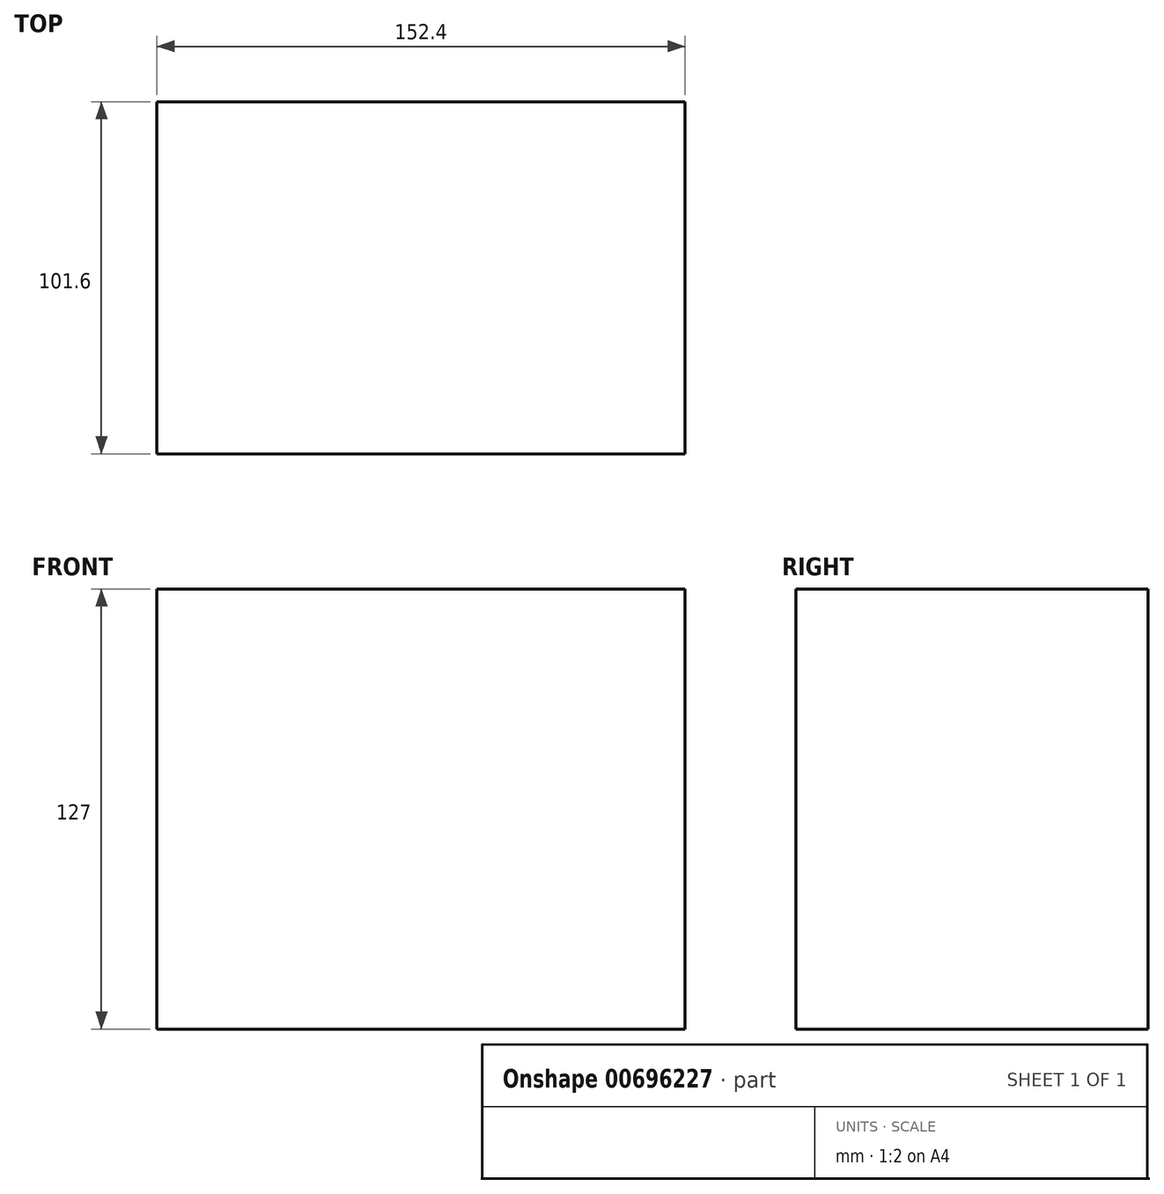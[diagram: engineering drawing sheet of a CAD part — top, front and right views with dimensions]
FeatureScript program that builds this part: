
annotation { "Feature Type Name" : "Feature", "Feature Type Description" : "" }
export const myFeature = defineFeature(function(context is Context, id is Id, definition is map)
    precondition{}
    {
        {
            var Q0;
            Q0=qCreatedBy(makeId("Front.planeOp"),FACE);
            var sketch = newSketch(context, id + "F0", { "sketchPlane" : qUnion([Q0])});
            skLineSegment(sketch, "E0", {"start": v(-76.03, 0) * mm, "end": v(76.37, 0) * mm});
            skLineSegment(sketch, "E1", {"start": v(-76.03, 0) * mm, "end": v(-76.03, 127) * mm});
            skLineSegment(sketch, "E2", {"start": v(-76.03, 127) * mm, "end": v(76.37, 127) * mm});
            skLineSegment(sketch, "E3", {"start": v(76.37, 127) * mm, "end": v(76.37, 0) * mm});
            skSolve(sketch);
        }
        {
            var Q0;
            Q0=makeQuery(id+"F0.imprint","IMPRINT",FACE,{"disambiguationData":[TD([[makeQuery(id+"F0.imprint","IMPRINT",EDGE,{"derivedFrom":sQuery(id+"F0.wireOp",EDGE,"E0")}),1.0]])]});
            extrude(context, id + "F1", {"entities" : qUnion([Q0]), "depth" : 101.6 * mm, "offsetDistance" : 25.4 * mm});
        }
    });
